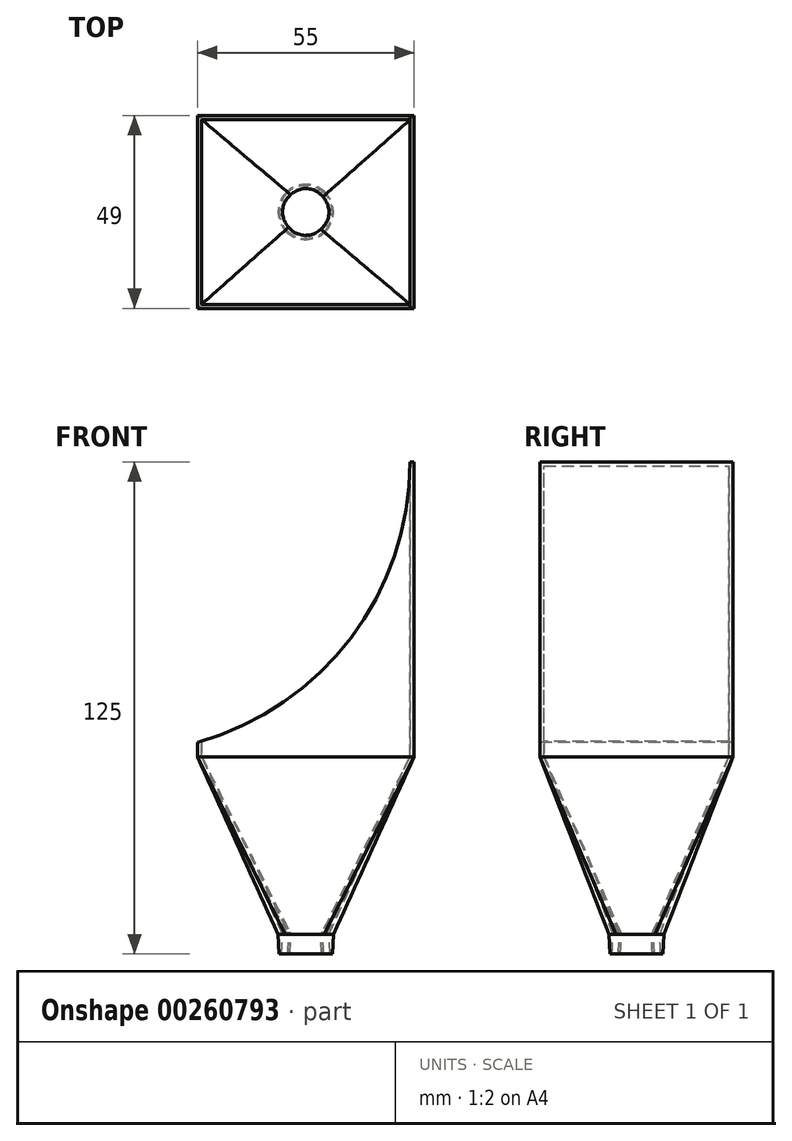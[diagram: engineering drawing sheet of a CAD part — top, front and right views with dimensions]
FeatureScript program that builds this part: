
annotation { "Feature Type Name" : "Feature", "Feature Type Description" : "" }
export const myFeature = defineFeature(function(context is Context, id is Id, definition is map)
    precondition{}
    {
        {
            var Q0;
            Q0=qCreatedBy(makeId("Top.planeOp"),FACE);
            var sketch = newSketch(context, id + "F0", { "sketchPlane" : qUnion([Q0])});
            skCircle(sketch, "E0", {"center": v(0, 0) * mm, "radius": 7 * mm});
            skSolve(sketch);
        }
        {
            var Q0;
            Q0=qCreatedBy(makeId("Top.planeOp"),FACE);
            cPlane(context, id + "F1", {"entities" : qUnion([Q0]), "cplaneType" : CPlaneType.OFFSET, "offset" : 120 * mm, "width" : 150 * mm, "height" : 150 * mm});
        }
        {
            var Q0;
            Q0=qCreatedBy(id+"F1.planeOp",FACE);
            var sketch = newSketch(context, id + "F2", { "sketchPlane" : qUnion([Q0])});
            skLineSegment(sketch, "E1.bottom", {"start": v(27.5, -24.5) * mm, "end": v(-27.5, -24.5) * mm});
            skLineSegment(sketch, "E1.top", {"start": v(27.5, 24.5) * mm, "end": v(-27.5, 24.5) * mm});
            skLineSegment(sketch, "E1.left", {"start": v(27.5, -24.5) * mm, "end": v(27.5, 24.5) * mm});
            skLineSegment(sketch, "E1.right", {"start": v(-27.5, -24.5) * mm, "end": v(-27.5, 24.5) * mm});
            skPoint(sketch, "E1.middle", {"position": v(0, 0) * mm});
            skSolve(sketch);
        }
        {
            var Q0;
            Q0=qCreatedBy(id+"F1.planeOp",FACE);
            cPlane(context, id + "F3", {"entities" : qUnion([Q0]), "cplaneType" : CPlaneType.OFFSET, "offset" : 75 * mm, "oppositeDirection" : true, "width" : 150 * mm, "height" : 150 * mm});
        }
        {
            var Q0;
            Q0=qCreatedBy(id+"F3.planeOp",FACE);
            var sketch = newSketch(context, id + "F4", { "sketchPlane" : qUnion([Q0])});
            skLineSegment(sketch, "E2.bottom", {"start": v(27.5, 24.5) * mm, "end": v(-27.5, 24.5) * mm});
            skLineSegment(sketch, "E2.top", {"start": v(27.5, -24.5) * mm, "end": v(-27.5, -24.5) * mm});
            skLineSegment(sketch, "E2.left", {"start": v(27.5, 24.5) * mm, "end": v(27.5, -24.5) * mm});
            skLineSegment(sketch, "E2.right", {"start": v(-27.5, 24.5) * mm, "end": v(-27.5, -24.5) * mm});
            skPoint(sketch, "E2.middle", {"position": v(0, 0) * mm});
            skSolve(sketch);
        }
        {
            var Q0;
            Q0=makeQuery(id+"F2.imprint","IMPRINT",FACE,{"disambiguationData":[TD([[makeQuery(id+"F2.imprint","IMPRINT",EDGE,{"derivedFrom":sQuery(id+"F2.wireOp",EDGE,"E1.bottom")}),-1.0]])]});
            var Q1;
            Q1=makeQuery(id+"F4.imprint","IMPRINT",FACE,{"disambiguationData":[TD([[makeQuery(id+"F4.imprint","IMPRINT",EDGE,{"derivedFrom":sQuery(id+"F4.wireOp",EDGE,"E2.bottom")}),1.0]])]});
            loft(context, id + "F5", {"sheetProfilesArray" : [{ "sheetProfileEntities" : qUnion([Q0]) }, { "sheetProfileEntities" : qUnion([Q1]) }]});
        }
        {
            var Q1;
            Q1=makeQuery(id+"F0.imprint","IMPRINT",FACE,{"disambiguationData":[TD([[makeQuery(id+"F0.imprint","IMPRINT",EDGE,{"derivedFrom":sQuery(id+"F0.wireOp",EDGE,"E0")}),1.0]])]});
            var Q2;
            Q2=makeQuery(id+"F5.opLoft","CAP_FACE",FACE,{"disambiguationData":[OSD([makeQuery(id+"F4.imprint","IMPRINT",FACE,{"disambiguationData":[TD([[makeQuery(id+"F4.imprint","IMPRINT",EDGE,{"derivedFrom":sQuery(id+"F4.wireOp",EDGE,"E2.bottom")}),1.0]])]})])],"isStart":true});
            loft(context, id + "F6", {"operationType" : NewBodyOperationType.ADD, "sheetProfilesArray" : [{ "sheetProfileEntities" : qUnion([Q1]) }, { "sheetProfileEntities" : qUnion([Q2]) }]});
        }
        {
            var Q0;
            Q0=makeQuery(id+"F10.boolean.opBoolean","COPY",FACE,{"derivedFrom":makeQuery(id+"F10.opExtrude","SWEPT_FACE",FACE,{"disambiguationData":[OSD([sQuery(id+"F9.wireOp",EDGE,"E3")])]})});
            var Q1;
            Q1=makeQuery(id+"F6.opLoft","CAP_FACE",FACE,{"disambiguationData":[OSD([makeQuery(id+"F0.imprint","IMPRINT",FACE,{"disambiguationData":[TD([[makeQuery(id+"F0.imprint","IMPRINT",EDGE,{"derivedFrom":sQuery(id+"F0.wireOp",EDGE,"E0")}),1.0]])]})])],"isStart":true});
            shell(context, id + "F7", {"entities" : qUnion([Q0, Q1]), "thickness" : 1 * mm});
        }
        {
            var Q0;
            Q0=makeQuery(id+"F6.opLoft","CAP_FACE",FACE,{"disambiguationData":[OSD([makeQuery(id+"F0.imprint","IMPRINT",FACE,{"disambiguationData":[TD([[makeQuery(id+"F0.imprint","IMPRINT",EDGE,{"derivedFrom":sQuery(id+"F0.wireOp",EDGE,"E0")}),1.0]])]})])],"isStart":true});
            extrude(context, id + "F8", {"entities" : qUnion([Q0]), "operationType" : NewBodyOperationType.ADD, "depth" : 5 * mm, "hasDraft" : true, "draftAngle" : 3 * degree, "draftPullDirection" : true});
        }
        {
            var Q0;
            Q0=qCreatedBy(makeId("Front.planeOp"),FACE);
            var sketch = newSketch(context, id + "F9", { "sketchPlane" : qUnion([Q0])});
            skCircle(sketch, "E3", {"center": v(-47.5, 120) * mm, "radius": 75 * mm});
            skCircle(sketch, "E4", {"center": v(-47.5, 120) * mm, "radius": 74 * mm});
            skSolve(sketch);
        }
        {
            var Q0;
            Q0=makeQuery(id+"F9.imprint","IMPRINT",FACE,{"disambiguationData":[TD([[makeQuery(id+"F9.imprint","IMPRINT",EDGE,{"derivedFrom":sQuery(id+"F9.wireOp",EDGE,"E4")}),1.0]])]});
            var Q1;
            Q1=sQuery(id+"F9.wireOp",EDGE,"E3");
            extrude(context, id + "F10", {"entities" : qUnion([Q0]), "operationType" : NewBodyOperationType.REMOVE, "surfaceEntities" : qUnion([Q1]), "oppositeDirection" : true, "depth" : 100 * mm, "hasSecondDirection" : true, "secondDirectionOppositeDirection" : false, "secondDirectionDepth" : 100 * mm});
        }
    });
